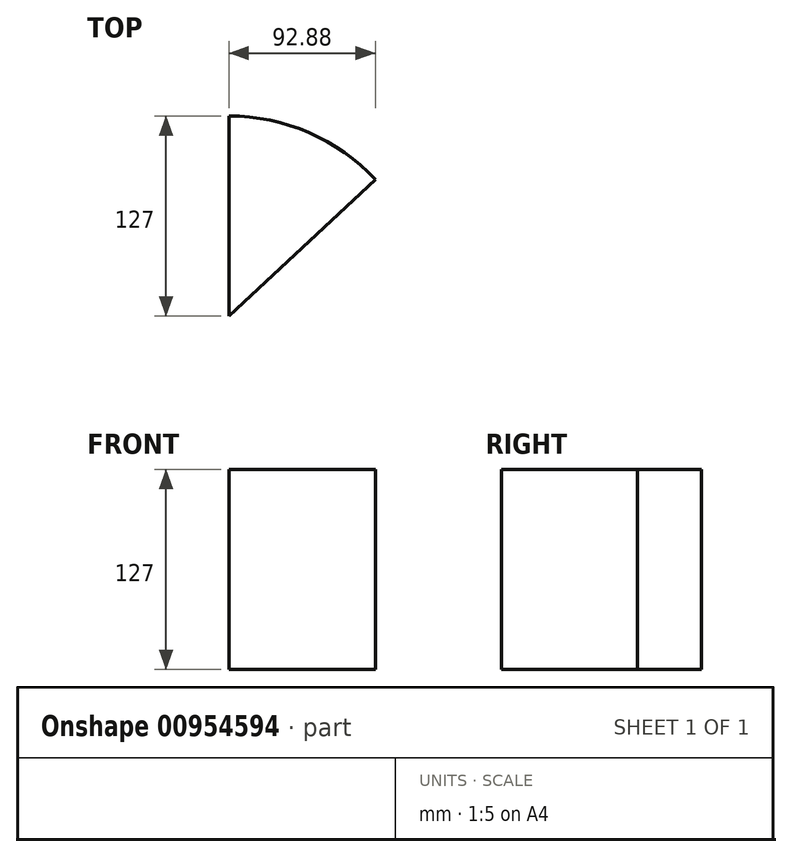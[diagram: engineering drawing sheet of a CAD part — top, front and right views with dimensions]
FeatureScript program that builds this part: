
annotation { "Feature Type Name" : "Feature", "Feature Type Description" : "" }
export const myFeature = defineFeature(function(context is Context, id is Id, definition is map)
    precondition{}
    {
        {
            var Q0;
            Q0=qCreatedBy(makeId("Top.planeOp"),FACE);
            var sketch = newSketch(context, id + "F0", { "sketchPlane" : qUnion([Q0])});
            skCircle(sketch, "E0", {"center": v(0, 0) * mm, "radius": 127 * mm});
            skSolve(sketch);
        }
        {
            var Q0;
            Q0=qCreatedBy(makeId("Top.planeOp"),FACE);
            var sketch = newSketch(context, id + "F1", { "sketchPlane" : qUnion([Q0])});
            skLineSegment(sketch, "E1", {"start": v(0, 0) * mm, "end": v(0, 127) * mm});
            skLineSegment(sketch, "E2", {"start": v(92.88, 86.61) * mm, "end": v(0, 0) * mm});
            skArc(sketch, "E3.0", {"start": v(92.88, 86.61) * mm, "mid": v(50.64, 116.47) * mm, "end": v(0, 127) * mm});
            skSolve(sketch);
        }
        {
            var Q0;
            Q0 = qSketchRegion(id + "F1", true);
            extrude(context, id + "F2", {"entities" : qUnion([Q0]), "depth" : 127 * mm, "offsetDistance" : 25.4 * mm});
        }
    });
